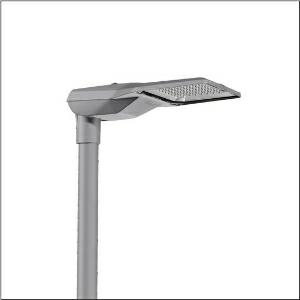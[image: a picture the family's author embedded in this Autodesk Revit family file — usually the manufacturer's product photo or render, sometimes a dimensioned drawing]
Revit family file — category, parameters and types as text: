
# Revit family: streetlight_sl_21_midi___stw1_0a_5xe3e33s08mb_c28b
name_source: partatom
category: Lighting Fixtures
units: mm (PartAtom-declared; Revit-internal decimal feet)

## family parameters
Cut with Voids When Loaded = No
Host = Face
Light Source = No
Part Type = Normal
Room Calculation Point = No
Round Connector Dimension = Use Diameter
Shared = No

## types (1)
- --- (1 x LED, 18270 lm, 136 W, 3000K)
    Apparent Load = 136 VA
    CIE Flux Codes = 38 75 98 100 100
    Color Rendering = 70
    Color Temperature = 3000K
    Default Elevation = 1800 mm
    Description = Streetlight SL 21 midi, mast luminaire, primary light control with lens, of PMMA, primary optical cover: cover, of toughened safety glass, transparent, light distribution: STW1.0a, light emission: direct distribution, primary light characteristic: asymmetric, installation type: side-entry, post-top, LED, High Power LED, rated luminous flux: 18.270lm, luminous efficacy: 134lm/W, light colour: 730, colour temperature: 3000K, control gear: D4i, control: overheat protection, constant luminous flux control, time-dependent luminous flux control, flexible luminous flux parameterisation, pre-setting: logarithmic dimming characteristic, mains connection: 230..240V, AC, 50/60Hz, start of lifetime: 136W, end of service life: 142W, reduction: 61W, luminaire housing, of diecast aluminium, powder-coated, SITECO metallic grey (DB 702S), corrosivity category C5 high according to DIN EN ISO 12944, please order mast flange separately, inclination adjustable: 0°, 5°, 10°, 15°, sealing non-destructively replaceable, multi-level sealing system, length: 644mm, width: 335mm, height: 110mm, mast flange for spigot size: 42mm (side-entry): 5XC10008XM4, 60/48mm (side-entry/post-top): 5XC10108XM2, 76/60mm (side-entry/post-top): 5XC10108XM1, mounting height: 4..8m, Smart Interface above, protection rating (complete): IP66, insulation class (complete): insulation class II (safety insulation), certification: CE, ENEC, ENEC+, VDE, impact resistance: IK10, permissible operating ambient temperature for outdoor applications: -40..+50°C, standard-compliant lighting for roads and squares, packaging unit: 1 piece

Light Distribution: STW1.0a
    Height = 111 mm
    Lamp = 1 x LED
    Lamp Light Flux = 18270 lm
    Lamp Power = 136 W
    Lamp count = 1
    Length = 644 mm
    Luminous efficacy = 134 lm/W
    Manufacturer = Siteco
    ModVariant = No
    Model = 5XE3E33S08MB
    Number of Poles = 1
    OnlyDefault = Yes
    Power Factor = 1
    Product Name = Streetlight SL 21 midi | STW1.0a
    Product group = mast luminaire | pylon top
    ProductGroupID = 6100
    Protection Class = Protection class II
    Protection Degree = IP 66
    RLX_Detail_Level = 1
    RLX_Emergency_Light_Flux = 0 lm
    RLX_Emergency_Type = 0
    RLX_Emergency_Type_DB = No
    RlxData = <blob elided: 26877 chars, md5=d88172ae>
    Socket = socket
    Standby Power = 0 W
    System Light Flux = 18270 lm
    System Power = 136 W
    Type Comments = factory setting: luminous flux: 100 % | dim-lin: 254 | 695 mA
    Type Image = l_1004302.jpg
    URL = http://relux.com
    VarID = @adj_185449
    Voltage = 0 V
    Weight = 0.00 kg
    Width = 336 mm

## geometry (parser evidence)
native form markers: Blend x4, Sweep x11
no freeform markers — native parametric forms only
